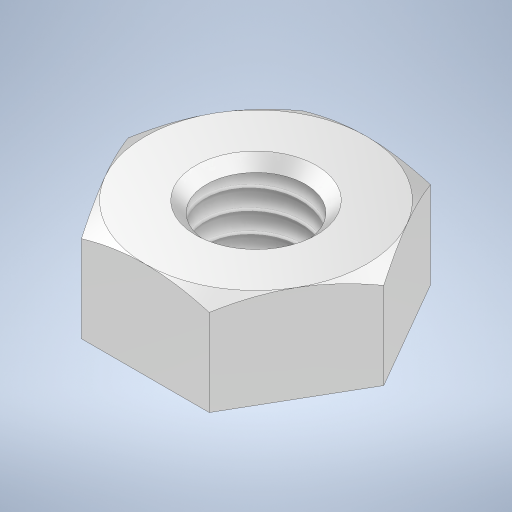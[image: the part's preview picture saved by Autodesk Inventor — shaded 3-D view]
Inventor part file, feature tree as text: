
AUTODESK INVENTOR PART (.ipt)
format: ipt  version: 2024.2 (Build 282272000, 272)  size: 283,136 bytes
history: native  units: mm
features: sketch x2, revolve x1, extrude x1, hole x1, mirror x1
ambient origin geometry x8: Origin, YZ Plane, XZ Plane, XY Plane, X Axis, Y Axis, Z Axis, Center Point
bodies: Solid1 (feature_tree)
feature tree (6):
  revolve  "Revolution1"  [1 undecoded]
  sketch  "Sketch2"  dims[d2=6.350853mm d3=30.0deg d4=90.0deg d5=0.0mm d6=0.0mm d7=2.459mm d8=6.0mm d9=3.0mm d10=2.0mm d11=90.0deg d12=6.0mm d13=0.0mm]
  extrude  "Extrusion1"  TaperAngle=30.0deg  [1 undecoded]
  hole  "Hole1"  [1 undecoded]
  mirror  "Mirror1"
  sketch  "Sketch1"  dims[d0=2.4mm d1=5.5mm]
note: 3 required parameter values undecoded (feature->parameter linkage not recoverable at this tier; creation-order binding heuristic only, values carry confidence <= 0.55)